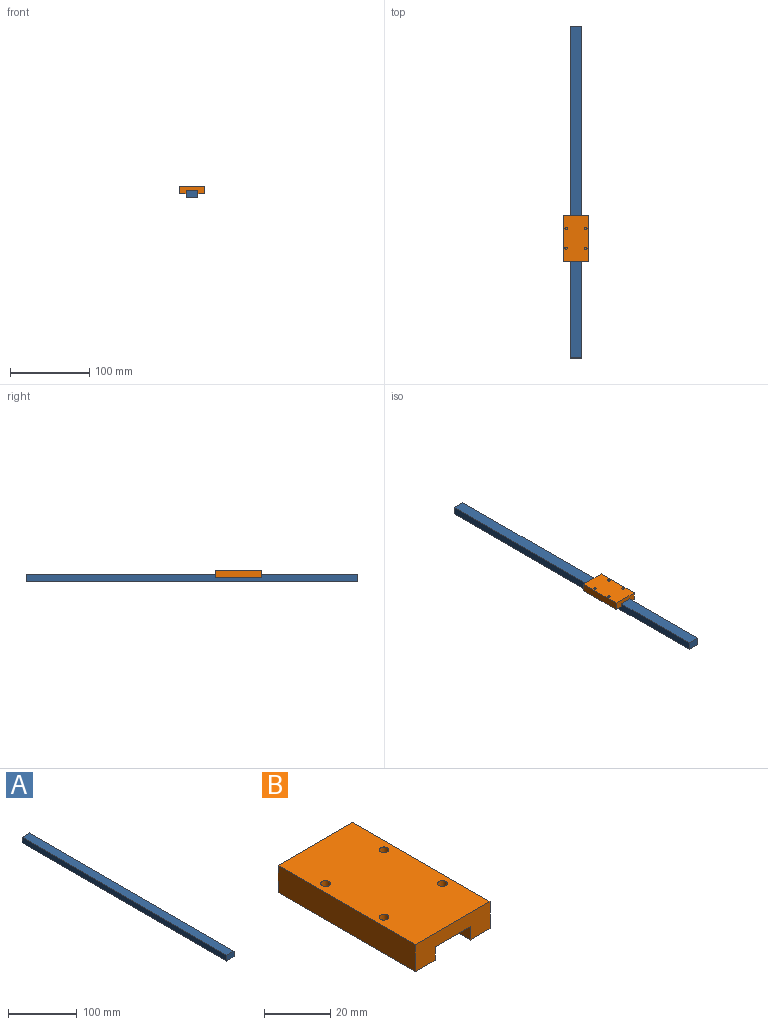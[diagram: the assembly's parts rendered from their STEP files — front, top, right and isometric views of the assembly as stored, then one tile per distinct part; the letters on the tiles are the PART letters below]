
ASSEMBLY  parts=2 mates=1
PART A: 6 faces, bbox 15x420x10 mm
  f0: plane 420x15mm, normal (0,0,-1), area 6300mm2, adj f1,f3,f4,f5
  f1: plane 420x10mm, normal (1,0,0), area 4200mm2, adj f0,f2,f4,f5
  f2: plane 420x15mm, normal (0,0,1), area 6300mm2, adj f1,f3,f4,f5
  f3: plane 420x10mm, normal (-1,0,0), area 4200mm2, adj f0,f2,f4,f5
  f4: plane 15x10mm, normal (0,-1,0), area 150mm2, adj f0,f1,f2,f3
  f5: plane 15x10mm, normal (0,1,0), area 150mm2, adj f0,f1,f2,f3
PART B: 18 faces, bbox 32x58.8x10 mm
  f0: plane 58.8x8.5mm, normal (0,0,-1), area 499.8mm2, adj f1,f7,f8,f9
  f1: plane 58.8x5mm, normal (1,0,0), area 294mm2, adj f0,f2,f8,f9
  f2: plane 58.8x15mm, normal (0,0,-1), area 882mm2, adj f1,f3,f8,f9
  f3: plane 58.8x5mm, normal (-1,0,0), area 294mm2, adj f2,f4,f8,f9
  f4: plane 58.8x8.5mm, normal (0,0,-1), area 499.8mm2, adj f3,f5,f8,f9
  f5: plane 58.8x10mm, normal (1,0,0), area 588mm2, adj f4,f6,f8,f9
  f6: plane 58.8x32mm, normal (0,0,1), area 1853.3mm2, adj f5,f7,f8,f9,f10,f12,f14,f16
  f7: plane 58.8x10mm, normal (-1,0,0), area 588mm2, adj f0,f6,f8,f9
  f8: plane 32x10mm, normal (0,-1,0), area 245mm2, adj f0,f1,f2,f3,f4,f5,f6,f7
  f9: plane 32x10mm, normal (0,1,0), area 245mm2, adj f0,f1,f2,f3,f4,f5,f6,f7
  f10: cylinder r=1.5mm len=3.5mm, axis (0,0,1), area 33mm2, adj f6,f11
  f11: plane 3x3mm, normal (0,0,1), area 7.1mm2, adj f10
  f12: cylinder r=1.5mm len=3.5mm, axis (0,0,1), area 33mm2, adj f6,f13
  f13: plane 3x3mm, normal (0,0,1), area 7.1mm2, adj f12
  f14: cylinder r=1.5mm len=3.5mm, axis (0,0,1), area 33mm2, adj f6,f15
  f15: plane 3x3mm, normal (0,0,1), area 7.1mm2, adj f14
  f16: cylinder r=1.5mm len=3.5mm, axis (0,0,1), area 33mm2, adj f6,f17
  f17: plane 3x3mm, normal (0,0,1), area 7.1mm2, adj f16
PLACE A t=(0,0,5)mm
PLACE B t=(0,-29.36,10)mm
MATE slider B.f8 <-> A.f4  axis (0,-1,0) through (-7.5,-88.16,10)mm
